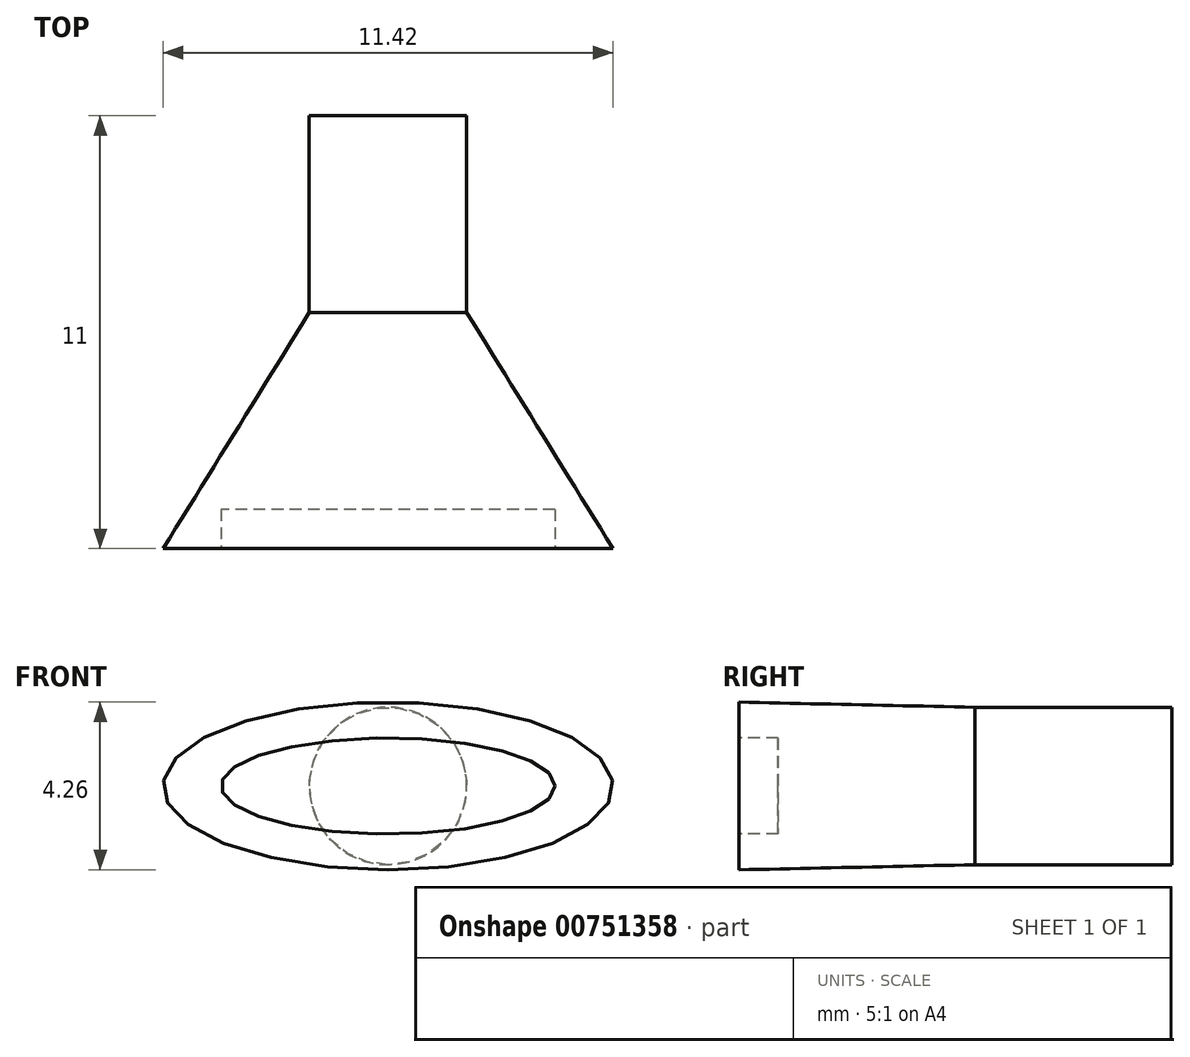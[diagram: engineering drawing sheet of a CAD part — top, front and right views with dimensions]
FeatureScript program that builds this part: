
annotation { "Feature Type Name" : "Feature", "Feature Type Description" : "" }
export const myFeature = defineFeature(function(context is Context, id is Id, definition is map)
    precondition{}
    {
        {
            var Q0;
            Q0=qCreatedBy(makeId("Front.planeOp"),FACE);
            var sketch = newSketch(context, id + "F0", { "sketchPlane" : qUnion([Q0])});
            skCircle(sketch, "E0", {"center": v(0, 0) * mm, "radius": 2 * mm});
            skSolve(sketch);
        }
        {
            var Q0;
            Q0=makeQuery(id+"F0.imprint","IMPRINT",FACE,{"disambiguationData":[TD([[makeQuery(id+"F0.imprint","IMPRINT",EDGE,{"derivedFrom":sQuery(id+"F0.wireOp",EDGE,"E0")}),1.0]])]});
            extrude(context, id + "F1", {"entities" : qUnion([Q0]), "depth" : 5 * mm, "offsetDistance" : 25 * mm});
        }
        {
            var Q0;
            Q0=makeQuery(id+"F1.opExtrude","CAP_FACE",FACE,{"disambiguationData":[OSD([sQuery(id+"F0.wireOp",EDGE,"E0")])],"isStart":false});
            var sketch = newSketch(context, id + "F2", { "sketchPlane" : qUnion([Q0])});
            skSolve(sketch);
        }
        {
            var Q0;
            Q0=qCreatedBy(makeId("Front.planeOp"),FACE);
            cPlane(context, id + "F3", {"entities" : qUnion([Q0]), "cplaneType" : CPlaneType.OFFSET, "offset" : 11 * mm, "width" : 150 * mm, "height" : 150 * mm});
        }
        {
            var Q0;
            Q0=qCreatedBy(id+"F3.planeOp",FACE);
            var sketch = newSketch(context, id + "F4", { "sketchPlane" : qUnion([Q0])});
            skEllipse(sketch, "E1", {"center": v(0, 0) * mm, "majorRadius": 5.71 * mm, "minorRadius": 2.13 * mm, "majorAxis": v(1, 0)});
            skSolve(sketch);
        }
        {
            var Q0;
            Q0=makeQuery(id+"F2.imprint","IMPRINT",FACE,{"disambiguationData":[TD([[makeQuery(id+"F2.imprint","IMPRINT",EDGE,{"derivedFrom":makeQuery(id+"F1.opExtrude","CAP_EDGE",EDGE,{"disambiguationData":[OSD([sQuery(id+"F0.wireOp",EDGE,"E0")])],"isStart":false})}),1.0]])]});
            var Q1;
            Q1=makeQuery(id+"F4.imprint","IMPRINT",FACE,{"disambiguationData":[TD([[makeQuery(id+"F4.imprint","IMPRINT",EDGE,{"derivedFrom":sQuery(id+"F4.wireOp",EDGE,"E1")}),1.0]])]});
            loft(context, id + "F5", {"operationType" : NewBodyOperationType.ADD, "sheetProfilesArray" : [{ "sheetProfileEntities" : qUnion([Q0]) }, { "sheetProfileEntities" : qUnion([Q1]) }]});
        }
        {
            var Q0;
            Q0=makeQuery(id+"F5.opLoft","CAP_FACE",FACE,{"disambiguationData":[OSD([makeQuery(id+"F4.imprint","IMPRINT",FACE,{"disambiguationData":[TD([[makeQuery(id+"F4.imprint","IMPRINT",EDGE,{"derivedFrom":sQuery(id+"F4.wireOp",EDGE,"E1")}),1.0]])]})])],"isStart":true});
            var sketch = newSketch(context, id + "F6", { "sketchPlane" : qUnion([Q0])});
            skEllipse(sketch, "E2", {"center": v(0, 0) * mm, "majorRadius": 4.24 * mm, "minorRadius": 1.22 * mm, "majorAxis": v(1, 0)});
            skSolve(sketch);
        }
        {
            var Q0;
            Q0=makeQuery(id+"F6.imprint","IMPRINT",FACE,{"disambiguationData":[TD([[makeQuery(id+"F6.imprint","IMPRINT",EDGE,{"derivedFrom":sQuery(id+"F6.wireOp",EDGE,"E2")}),1.0]])]});
            extrude(context, id + "F7", {"entities" : qUnion([Q0]), "operationType" : NewBodyOperationType.REMOVE, "oppositeDirection" : true, "depth" : 1 * mm, "offsetDistance" : 25 * mm});
        }
    });
